# Revit family: External block S252_S450_3R1A
name_source: partatom
category: Оборудование
units: mm (PartAtom-declared; Revit-internal decimal feet)

## family parameters
Всегда вертикально = Да
Классификация = Нет
На основе рабочей плоскости = Нет
Общий = Нет
При загрузке вырезать с полостями = Нет
Размер круглого соединителя = Использовать диаметр
Тип детали = Нормальный
Точка принадлежности помещению = Нет

## types (5) — shared parameters
00_20_Manufacturer = BLAUBERG
00_20_Name = External block
B = 400 мм
C = 1740 мм
Casing Material = Steel, white, mat
Cp = 740 мм
Cv = 420 мм
D = 586 мм
Dv = 690 мм
E = 840 мм
Electric = Нет
Grid Material = Mesh, steel, painted,  white
Height = 1740 мм
Load Classification = HVAC
Maintenance zone material = <По категории>
Maximum Air Flow = 0.0 л/с
Width = 400 мм
h = 1720 мм
rn = 10 мм
wn = 268 мм
Изготовитель = BLAUBERG
zero-valued in all types: Отметка по умолчанию

## per-type parameters (varying)
| type | A | Lb | Length | Lv | Power | Weight | d | d1 |
| BLHVE-S252-O/3R1A | 1020 мм | 990 мм | 1020 мм | 100 мм | 4980 Вт | 228.00 кг | 13 мм | 22 мм |
| BLHVE-S280-O/3R1A | 1020 мм | 990 мм | 1020 мм | 100 мм | 5860 Вт | 228.00 кг | 13 мм | 22 мм |
| BLHVE-S335-O/3R1A | 1020 мм | 990 мм | 1020 мм | 100 мм | 7350 Вт | 230.00 кг | 13 мм | 22 мм |
| BLHVE-S400-O/3R1A | 1370 мм | 1340 мм | 1370 мм | 275 мм | 9340 Вт | 275.00 кг | 16 мм | 29 мм |
| BLHVE-S450-O/3R1A | 1370 мм | 1340 мм | 1370 мм | 275 мм | 10870 Вт | 275.00 кг | 16 мм | 29 мм |

note: column(s) folded — value = type name in every type: 00_20_Type
